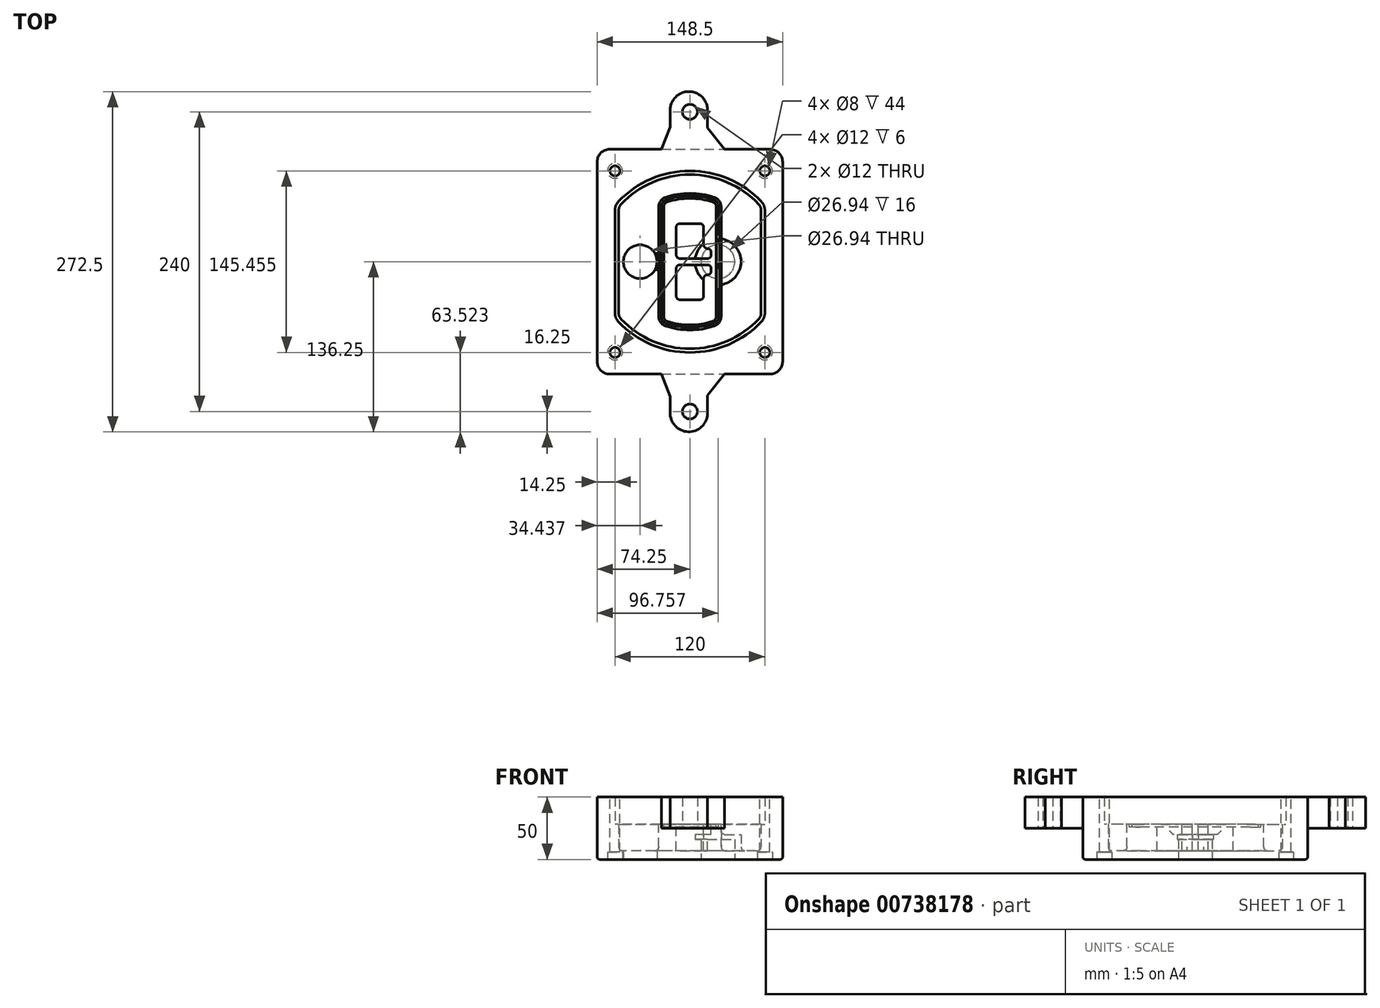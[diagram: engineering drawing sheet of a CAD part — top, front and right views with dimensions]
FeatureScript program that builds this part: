
annotation { "Feature Type Name" : "Feature", "Feature Type Description" : "" }
export const myFeature = defineFeature(function(context is Context, id is Id, definition is map)
    precondition{}
    {
        {
            var Q0;
            Q0=qCreatedBy(makeId("Top.planeOp"),FACE);
            var sketch = newSketch(context, id + "F0", { "sketchPlane" : qUnion([Q0])});
            skPoint(sketch, "E0.rect.middle", {"position": v(0, 0) * mm});
            skLineSegment(sketch, "E1.bottom", {"start": v(-64.25, -90) * mm, "end": v(64.25, -90) * mm});
            skLineSegment(sketch, "E1.top", {"start": v(-64.25, 90) * mm, "end": v(64.25, 90) * mm});
            skLineSegment(sketch, "E1.left", {"start": v(-74.25, -80) * mm, "end": v(-74.25, 80) * mm});
            skLineSegment(sketch, "E1.right", {"start": v(74.25, -80) * mm, "end": v(74.25, 80) * mm});
            skLineSegment(sketch, "E2", {"start": v(-74.25, 90) * mm, "end": v(74.25, -90) * mm, "construction": true});
            skLineSegment(sketch, "E3", {"start": v(74.25, 90) * mm, "end": v(-74.25, -90) * mm, "construction": true});
            skCircle(sketch, "E4", {"center": v(-60, 72.73) * mm, "radius": 4 * mm});
            skCircle(sketch, "E5", {"center": v(60, 72.73) * mm, "radius": 4 * mm});
            skCircle(sketch, "E6", {"center": v(60, -72.73) * mm, "radius": 4 * mm});
            skCircle(sketch, "E7", {"center": v(-60, -72.73) * mm, "radius": 4 * mm});
            skLineSegment(sketch, "E8", {"start": v(-60, 72.73) * mm, "end": v(60, 72.73) * mm, "construction": true});
            skLineSegment(sketch, "E9", {"start": v(60, 72.73) * mm, "end": v(60, -72.73) * mm, "construction": true});
            skLineSegment(sketch, "E10", {"start": v(60, -72.73) * mm, "end": v(-60, -72.73) * mm, "construction": true});
            skLineSegment(sketch, "E11", {"start": v(-60, -72.73) * mm, "end": v(-60, 72.73) * mm, "construction": true});
            skLineSegment(sketch, "E12", {"start": v(-60, 41.18) * mm, "end": v(-60, -41.18) * mm});
            skLineSegment(sketch, "E13", {"start": v(60, 41.18) * mm, "end": v(60, -41.18) * mm});
            skArc(sketch, "E14", {"start": v(57.27, 48.05) * mm, "mid": v(0, 72.73) * mm, "end": v(-57.27, 48.05) * mm});
            skArc(sketch, "E15", {"start": v(-57.27, -48.05) * mm, "mid": v(0, -72.73) * mm, "end": v(57.27, -48.05) * mm});
            skLineSegment(sketch, "E16", {"start": v(-60, 0) * mm, "end": v(60, 0) * mm, "construction": true});
            skPoint(sketch, "E17.visualSharp", {"position": v(-60, -45) * mm});
            skArc(sketch, "E17.filletArc", {"start": v(-60, -41.18) * mm, "mid": v(-59.3, -44.87) * mm, "end": v(-57.27, -48.05) * mm});
            skPoint(sketch, "E18.visualSharp", {"position": v(-60, 45) * mm});
            skArc(sketch, "E18.filletArc", {"start": v(-57.27, 48.05) * mm, "mid": v(-59.3, 44.87) * mm, "end": v(-60, 41.18) * mm});
            skPoint(sketch, "E19.visualSharp", {"position": v(60, 45) * mm});
            skArc(sketch, "E19.filletArc", {"start": v(60, 41.18) * mm, "mid": v(59.3, 44.87) * mm, "end": v(57.27, 48.05) * mm});
            skPoint(sketch, "E20.visualSharp", {"position": v(60, -45) * mm});
            skArc(sketch, "E20.filletArc", {"start": v(57.27, -48.05) * mm, "mid": v(59.3, -44.87) * mm, "end": v(60, -41.18) * mm});
            skPoint(sketch, "E21.visualSharp", {"position": v(-74.25, 90) * mm});
            skArc(sketch, "E21.filletArc", {"start": v(-64.25, 90) * mm, "mid": v(-71.32, 87.07) * mm, "end": v(-74.25, 80) * mm});
            skPoint(sketch, "E22.visualSharp", {"position": v(74.25, 90) * mm});
            skArc(sketch, "E22.filletArc", {"start": v(74.25, 80) * mm, "mid": v(71.32, 87.07) * mm, "end": v(64.25, 90) * mm});
            skPoint(sketch, "E23.visualSharp", {"position": v(74.25, -90) * mm});
            skArc(sketch, "E23.filletArc", {"start": v(64.25, -90) * mm, "mid": v(71.32, -87.07) * mm, "end": v(74.25, -80) * mm});
            skPoint(sketch, "E24.visualSharp", {"position": v(-74.25, -90) * mm});
            skArc(sketch, "E24.filletArc", {"start": v(-74.25, -80) * mm, "mid": v(-71.32, -87.07) * mm, "end": v(-64.25, -90) * mm});
            skArc(sketch, "E25.0", {"start": v(57, 41.18) * mm, "mid": v(56.5, 43.76) * mm, "end": v(55.09, 45.99) * mm});
            skLineSegment(sketch, "E25.1", {"start": v(57, 41.18) * mm, "end": v(57, -41.18) * mm});
            skArc(sketch, "E25.2", {"start": v(55.09, -45.99) * mm, "mid": v(56.5, -43.76) * mm, "end": v(57, -41.18) * mm});
            skArc(sketch, "E25.3", {"start": v(-55.09, -45.99) * mm, "mid": v(0, -69.73) * mm, "end": v(55.09, -45.99) * mm});
            skArc(sketch, "E25.4", {"start": v(-57, -41.18) * mm, "mid": v(-56.5, -43.76) * mm, "end": v(-55.09, -45.99) * mm});
            skArc(sketch, "E25.5", {"start": v(55.09, 45.99) * mm, "mid": v(0, 69.73) * mm, "end": v(-55.09, 45.99) * mm});
            skLineSegment(sketch, "E25.6", {"start": v(-57, 41.18) * mm, "end": v(-57, -41.18) * mm});
            skArc(sketch, "E25.7", {"start": v(-55.09, 45.99) * mm, "mid": v(-56.5, 43.76) * mm, "end": v(-57, 41.18) * mm});
            skArc(sketch, "E26.0", {"start": v(-60.18, 50.8) * mm, "mid": v(-63, 46.35) * mm, "end": v(-64, 41.18) * mm});
            skArc(sketch, "E26.1", {"start": v(60.18, 50.8) * mm, "mid": v(0, 76.73) * mm, "end": v(-60.18, 50.8) * mm});
            skArc(sketch, "E26.2", {"start": v(64, 41.18) * mm, "mid": v(63, 46.35) * mm, "end": v(60.18, 50.8) * mm});
            skLineSegment(sketch, "E26.3", {"start": v(64, 41.18) * mm, "end": v(64, -41.18) * mm});
            skArc(sketch, "E26.4", {"start": v(60.18, -50.8) * mm, "mid": v(63, -46.35) * mm, "end": v(64, -41.18) * mm});
            skLineSegment(sketch, "E26.5", {"start": v(-64, 41.18) * mm, "end": v(-64, -41.18) * mm});
            skArc(sketch, "E26.6", {"start": v(-60.18, -50.8) * mm, "mid": v(0, -76.73) * mm, "end": v(60.18, -50.8) * mm});
            skArc(sketch, "E26.7", {"start": v(-64, -41.18) * mm, "mid": v(-63, -46.35) * mm, "end": v(-60.18, -50.8) * mm});
            skSolve(sketch);
        }
        {
            var Q0;
            Q0=makeQuery(id+"F0.imprint","IMPRINT",FACE,{"disambiguationData":[TD([[makeQuery(id+"F0.imprint","IMPRINT",EDGE,{"derivedFrom":sQuery(id+"F0.wireOp",EDGE,"E1.bottom")}),1.0]])]});
            var Q1;
            Q1=makeQuery(id+"F0.imprint","IMPRINT",FACE,{"disambiguationData":[TD([[makeQuery(id+"F0.imprint","IMPRINT",EDGE,{"derivedFrom":sQuery(id+"F0.wireOp",EDGE,"E12")}),1.0]])]});
            var Q2;
            Q2=makeQuery(id+"F0.imprint","IMPRINT",FACE,{"disambiguationData":[TD([[makeQuery(id+"F0.imprint","IMPRINT",EDGE,{"derivedFrom":sQuery(id+"F0.wireOp",EDGE,"E25.0")}),1.0]])]});
            var Q3;
            Q3=makeQuery(id+"F0.imprint","IMPRINT",FACE,{"disambiguationData":[TD([[makeQuery(id+"F0.imprint","IMPRINT",EDGE,{"derivedFrom":sQuery(id+"F0.wireOp",EDGE,"E12")}),-1.0]])]});
            extrude(context, id + "F1", {"entities" : qUnion([Q0, Q1, Q2, Q3]), "oppositeDirection" : true, "depth" : 25 * mm});
        }
        {
            var Q0;
            Q0=makeQuery(id+"F0.imprint","IMPRINT",FACE,{"disambiguationData":[TD([[makeQuery(id+"F0.imprint","IMPRINT",EDGE,{"derivedFrom":sQuery(id+"F0.wireOp",EDGE,"E12")}),1.0]])]});
            extrude(context, id + "F2", {"entities" : qUnion([Q0]), "operationType" : NewBodyOperationType.ADD, "depth" : 3 * mm});
        }
        {
            var Q0;
            Q0=makeQuery(id+"F0.imprint","IMPRINT",FACE,{"disambiguationData":[TD([[makeQuery(id+"F0.imprint","IMPRINT",EDGE,{"derivedFrom":sQuery(id+"F0.wireOp",EDGE,"E25.0")}),1.0]])]});
            extrude(context, id + "F3", {"entities" : qUnion([Q0]), "operationType" : NewBodyOperationType.REMOVE, "oppositeDirection" : true, "depth" : 18 * mm});
        }
        {
            var Q0;
            Q0=makeQuery(id+"F2.opExtrude","CAP_FACE",FACE,{"disambiguationData":[OSD([sQuery(id+"F0.wireOp",EDGE,"E12"),sQuery(id+"F0.wireOp",EDGE,"E13"),sQuery(id+"F0.wireOp",EDGE,"E14"),sQuery(id+"F0.wireOp",EDGE,"E15"),sQuery(id+"F0.wireOp",EDGE,"E17.filletArc"),sQuery(id+"F0.wireOp",EDGE,"E18.filletArc"),sQuery(id+"F0.wireOp",EDGE,"E19.filletArc"),sQuery(id+"F0.wireOp",EDGE,"E20.filletArc"),sQuery(id+"F0.wireOp",EDGE,"E25.0"),sQuery(id+"F0.wireOp",EDGE,"E25.1"),sQuery(id+"F0.wireOp",EDGE,"E25.2"),sQuery(id+"F0.wireOp",EDGE,"E25.3"),sQuery(id+"F0.wireOp",EDGE,"E25.4"),sQuery(id+"F0.wireOp",EDGE,"E25.5"),sQuery(id+"F0.wireOp",EDGE,"E25.6"),sQuery(id+"F0.wireOp",EDGE,"E25.7")])],"isStart":false});
            var sketch = newSketch(context, id + "F4", { "sketchPlane" : qUnion([Q0])});
            skArc(sketch, "E27.0", {"start": v(-19.58, -51.49) * mm, "mid": v(0, -54.73) * mm, "end": v(19.58, -51.49) * mm});
            skArc(sketch, "E28.0", {"start": v(19.58, 51.49) * mm, "mid": v(0, 54.73) * mm, "end": v(-19.58, 51.49) * mm});
            skLineSegment(sketch, "E29", {"start": v(-25, 43.91) * mm, "end": v(-25, -43.91) * mm});
            skLineSegment(sketch, "E30", {"start": v(25, 43.91) * mm, "end": v(25, -43.91) * mm});
            skLineSegment(sketch, "E31", {"start": v(-25, 49.35) * mm, "end": v(25, 49.35) * mm, "construction": true});
            skLineSegment(sketch, "E32", {"start": v(-25, -49.35) * mm, "end": v(25, -49.35) * mm, "construction": true});
            skPoint(sketch, "E33.visualSharp", {"position": v(-25, 49.35) * mm});
            skArc(sketch, "E33.filletArc", {"start": v(-19.58, 51.49) * mm, "mid": v(-23.5, 48.57) * mm, "end": v(-25, 43.91) * mm});
            skPoint(sketch, "E34.visualSharp", {"position": v(25, 49.35) * mm});
            skArc(sketch, "E34.filletArc", {"start": v(25, 43.91) * mm, "mid": v(23.5, 48.57) * mm, "end": v(19.58, 51.49) * mm});
            skPoint(sketch, "E35.visualSharp", {"position": v(25, -49.35) * mm});
            skArc(sketch, "E35.filletArc", {"start": v(19.58, -51.49) * mm, "mid": v(23.5, -48.57) * mm, "end": v(25, -43.91) * mm});
            skPoint(sketch, "E36.visualSharp", {"position": v(-25, -49.35) * mm});
            skArc(sketch, "E36.filletArc", {"start": v(-25, -43.91) * mm, "mid": v(-23.5, -48.57) * mm, "end": v(-19.58, -51.49) * mm});
            skArc(sketch, "E37.0", {"start": v(55.09, 45.99) * mm, "mid": v(0, 69.73) * mm, "end": v(-55.09, 45.99) * mm});
            skArc(sketch, "E37.1", {"start": v(-55.09, 45.99) * mm, "mid": v(-56.5, 43.76) * mm, "end": v(-57, 41.18) * mm});
            skLineSegment(sketch, "E37.2", {"start": v(-57, 41.18) * mm, "end": v(-57, -41.18) * mm});
            skArc(sketch, "E37.3", {"start": v(-57, -41.18) * mm, "mid": v(-56.5, -43.76) * mm, "end": v(-55.09, -45.99) * mm});
            skArc(sketch, "E37.4", {"start": v(-55.09, -45.99) * mm, "mid": v(0, -69.73) * mm, "end": v(55.09, -45.99) * mm});
            skArc(sketch, "E37.5", {"start": v(55.09, -45.99) * mm, "mid": v(56.5, -43.76) * mm, "end": v(57, -41.18) * mm});
            skLineSegment(sketch, "E37.6", {"start": v(57, 41.18) * mm, "end": v(57, -41.18) * mm});
            skArc(sketch, "E37.7", {"start": v(57, 41.18) * mm, "mid": v(56.5, 43.76) * mm, "end": v(55.09, 45.99) * mm});
            skLineSegment(sketch, "E38.0", {"start": v(23, 43.91) * mm, "end": v(23, -43.91) * mm});
            skArc(sketch, "E38.1", {"start": v(18.93, -49.6) * mm, "mid": v(21.88, -47.4) * mm, "end": v(23, -43.91) * mm});
            skArc(sketch, "E38.2", {"start": v(-18.93, -49.6) * mm, "mid": v(0, -52.73) * mm, "end": v(18.93, -49.6) * mm});
            skArc(sketch, "E38.3", {"start": v(-23, -43.91) * mm, "mid": v(-21.88, -47.4) * mm, "end": v(-18.93, -49.6) * mm});
            skLineSegment(sketch, "E38.4", {"start": v(-23, 43.91) * mm, "end": v(-23, -43.91) * mm});
            skArc(sketch, "E38.5", {"start": v(23, 43.91) * mm, "mid": v(21.88, 47.4) * mm, "end": v(18.93, 49.6) * mm});
            skArc(sketch, "E38.6", {"start": v(-18.93, 49.6) * mm, "mid": v(-21.88, 47.4) * mm, "end": v(-23, 43.91) * mm});
            skArc(sketch, "E38.7", {"start": v(18.93, 49.6) * mm, "mid": v(0, 52.73) * mm, "end": v(-18.93, 49.6) * mm});
            skArc(sketch, "E39.0", {"start": v(21, 43.91) * mm, "mid": v(20.25, 46.24) * mm, "end": v(18.29, 47.7) * mm});
            skLineSegment(sketch, "E39.1", {"start": v(21, 43.91) * mm, "end": v(21, -43.91) * mm});
            skArc(sketch, "E39.2", {"start": v(18.29, -47.7) * mm, "mid": v(20.25, -46.24) * mm, "end": v(21, -43.91) * mm});
            skArc(sketch, "E39.3", {"start": v(-18.29, -47.7) * mm, "mid": v(0, -50.73) * mm, "end": v(18.29, -47.7) * mm});
            skArc(sketch, "E39.4", {"start": v(-21, -43.91) * mm, "mid": v(-20.25, -46.24) * mm, "end": v(-18.29, -47.7) * mm});
            skArc(sketch, "E39.5", {"start": v(18.29, 47.7) * mm, "mid": v(0, 50.73) * mm, "end": v(-18.29, 47.7) * mm});
            skLineSegment(sketch, "E39.6", {"start": v(-21, 43.91) * mm, "end": v(-21, -43.91) * mm});
            skArc(sketch, "E39.7", {"start": v(-18.29, 47.7) * mm, "mid": v(-20.25, 46.24) * mm, "end": v(-21, 43.91) * mm});
            skLineSegment(sketch, "E40", {"start": v(-25, 0) * mm, "end": v(25, 0) * mm, "construction": true});
            skLineSegment(sketch, "E41", {"start": v(-11, 5.5) * mm, "end": v(-11, 27.5) * mm});
            skLineSegment(sketch, "E42", {"start": v(-8, 30.5) * mm, "end": v(8, 30.5) * mm});
            skLineSegment(sketch, "E43", {"start": v(11, 27.5) * mm, "end": v(11, 13.5) * mm});
            skLineSegment(sketch, "E44", {"start": v(14, 10.5) * mm, "end": v(14, 10.5) * mm});
            skLineSegment(sketch, "E45", {"start": v(17, 7.5) * mm, "end": v(17, 5.5) * mm});
            skLineSegment(sketch, "E46", {"start": v(14, 2.5) * mm, "end": v(-8, 2.5) * mm});
            skPoint(sketch, "E47.visualSharp", {"position": v(-11, 30.5) * mm});
            skArc(sketch, "E47.filletArc", {"start": v(-8, 30.5) * mm, "mid": v(-10.12, 29.62) * mm, "end": v(-11, 27.5) * mm});
            skPoint(sketch, "E48.visualSharp", {"position": v(11, 30.5) * mm});
            skArc(sketch, "E48.filletArc", {"start": v(11, 27.5) * mm, "mid": v(10.12, 29.62) * mm, "end": v(8, 30.5) * mm});
            skPoint(sketch, "E49.visualSharp", {"position": v(11, 10.5) * mm});
            skArc(sketch, "E49.filletArc", {"start": v(11, 13.5) * mm, "mid": v(11.88, 11.38) * mm, "end": v(14, 10.5) * mm});
            skPoint(sketch, "E50.visualSharp", {"position": v(17, 10.5) * mm});
            skArc(sketch, "E50.filletArc", {"start": v(17, 7.5) * mm, "mid": v(16.12, 9.62) * mm, "end": v(14, 10.5) * mm});
            skPoint(sketch, "E51.visualSharp", {"position": v(17, 2.5) * mm});
            skArc(sketch, "E51.filletArc", {"start": v(14, 2.5) * mm, "mid": v(16.12, 3.38) * mm, "end": v(17, 5.5) * mm});
            skPoint(sketch, "E52.visualSharp", {"position": v(-11, 2.5) * mm});
            skArc(sketch, "E52.filletArc", {"start": v(-11, 5.5) * mm, "mid": v(-10.12, 3.38) * mm, "end": v(-8, 2.5) * mm});
            skLineSegment(sketch, "E53.0.MirrorCS", {"start": v(14, -2.5) * mm, "end": v(-8, -2.5) * mm});
            skArc(sketch, "E54.0.MirrorCS", {"start": v(-11, -5.5) * mm, "mid": v(-10.12, -3.38) * mm, "end": v(-8, -2.5) * mm});
            skLineSegment(sketch, "E55.0.MirrorCS", {"start": v(-11, -5.5) * mm, "end": v(-11, -27.5) * mm});
            skArc(sketch, "E56.0.MirrorCS", {"start": v(-8, -30.5) * mm, "mid": v(-10.12, -29.62) * mm, "end": v(-11, -27.5) * mm});
            skLineSegment(sketch, "E57.0.MirrorCS", {"start": v(-8, -30.5) * mm, "end": v(8, -30.5) * mm});
            skArc(sketch, "E58.0.MirrorCS", {"start": v(11, -27.5) * mm, "mid": v(10.12, -29.62) * mm, "end": v(8, -30.5) * mm});
            skLineSegment(sketch, "E59.0.MirrorCS", {"start": v(11, -27.5) * mm, "end": v(11, -13.5) * mm});
            skArc(sketch, "E60.0.MirrorCS", {"start": v(11, -13.5) * mm, "mid": v(11.88, -11.38) * mm, "end": v(14, -10.5) * mm});
            skArc(sketch, "E61.0.MirrorCS", {"start": v(17, -7.5) * mm, "mid": v(16.12, -9.62) * mm, "end": v(14, -10.5) * mm});
            skLineSegment(sketch, "E62.0.MirrorCS", {"start": v(17, -7.5) * mm, "end": v(17, -5.5) * mm});
            skArc(sketch, "E63.0.MirrorCS", {"start": v(14, -2.5) * mm, "mid": v(16.12, -3.38) * mm, "end": v(17, -5.5) * mm});
            skSolve(sketch);
        }
        {
            var Q0;
            Q0=makeQuery(id+"F4.imprint","IMPRINT",FACE,{"disambiguationData":[TD([[makeQuery(id+"F4.imprint","IMPRINT",EDGE,{"derivedFrom":sQuery(id+"F4.wireOp",EDGE,"E27.0")}),1.0]])]});
            var Q1;
            Q1=makeQuery(id+"F4.imprint","IMPRINT",FACE,{"disambiguationData":[TD([[makeQuery(id+"F4.imprint","IMPRINT",EDGE,{"derivedFrom":sQuery(id+"F4.wireOp",EDGE,"E38.0")}),-1.0]])]});
            var Q2;
            Q2=makeQuery(id+"F4.imprint","IMPRINT",FACE,{"disambiguationData":[TD([[makeQuery(id+"F4.imprint","IMPRINT",EDGE,{"derivedFrom":sQuery(id+"F4.wireOp",EDGE,"E39.0")}),1.0]])]});
            extrude(context, id + "F5", {"entities" : qUnion([Q0, Q1, Q2]), "operationType" : NewBodyOperationType.ADD, "endBound" : BoundingType.UP_TO_NEXT, "oppositeDirection" : true, "depth" : 25 * mm});
        }
        {
            var Q0;
            Q0=makeQuery(id+"F4.imprint","IMPRINT",FACE,{"disambiguationData":[TD([[makeQuery(id+"F4.imprint","IMPRINT",EDGE,{"derivedFrom":sQuery(id+"F4.wireOp",EDGE,"E38.0")}),-1.0]])]});
            extrude(context, id + "F6", {"entities" : qUnion([Q0]), "operationType" : NewBodyOperationType.REMOVE, "oppositeDirection" : true, "depth" : 2 * mm});
        }
        {
            var Q0;
            Q0=makeQuery(id+"F1.opExtrude","CAP_FACE",FACE,{"disambiguationData":[OSD([sQuery(id+"F0.wireOp",EDGE,"E1.bottom"),sQuery(id+"F0.wireOp",EDGE,"E1.top"),sQuery(id+"F0.wireOp",EDGE,"E1.left"),sQuery(id+"F0.wireOp",EDGE,"E1.right"),sQuery(id+"F0.wireOp",EDGE,"E4"),sQuery(id+"F0.wireOp",EDGE,"E5"),sQuery(id+"F0.wireOp",EDGE,"E6"),sQuery(id+"F0.wireOp",EDGE,"E7"),sQuery(id+"F0.wireOp",EDGE,"E21.filletArc"),sQuery(id+"F0.wireOp",EDGE,"E22.filletArc"),sQuery(id+"F0.wireOp",EDGE,"E23.filletArc"),sQuery(id+"F0.wireOp",EDGE,"E24.filletArc")])],"isStart":false});
            var sketch = newSketch(context, id + "F7", { "sketchPlane" : qUnion([Q0])});
            skCircle(sketch, "E64", {"center": v(22.5, 0) * mm, "radius": 13.47 * mm});
            skCircle(sketch, "E65", {"center": v(-39.81, 0) * mm, "radius": 13.47 * mm});
            skLineSegment(sketch, "E66", {"start": v(74.25, 0) * mm, "end": v(-74.25, 0) * mm});
            skCircle(sketch, "E67", {"center": v(22.5, 0) * mm, "radius": 18.47 * mm});
            skCircle(sketch, "E68", {"center": v(60, -72.73) * mm, "radius": 6 * mm});
            skCircle(sketch, "E69", {"center": v(-60, -72.73) * mm, "radius": 6 * mm});
            skCircle(sketch, "E70", {"center": v(-60, 72.73) * mm, "radius": 6 * mm});
            skCircle(sketch, "E71", {"center": v(60, 72.73) * mm, "radius": 6 * mm});
            skSolve(sketch);
        }
        {
            var Q0;
            {var subQ1=sQuery(id+"F7.wireOp",EDGE,"E66");var subQ4=sQuery(id+"F7.wireOp",EDGE,"E64");var subQ6=makeQuery(id+"F7.imprint","INTERSECT",VERTEX,{"disambiguationData":[OD(0.0)],"derivedFrom":[subQ4,subQ1]});Q0=makeQuery(id+"F7.imprint","IMPRINT",FACE,{"disambiguationData":[TD([[makeQuery(id+"F7.imprint","IMPRINT",EDGE,{"disambiguationData":[TD([[subQ6,-1.0]])],"derivedFrom":subQ4}),-1.0]])]});}
            var Q1;
            {var subQ0=sQuery(id+"F7.wireOp",EDGE,"E66");var subQ1=sQuery(id+"F7.wireOp",EDGE,"E64");var subQ3=makeQuery(id+"F7.imprint","INTERSECT",VERTEX,{"disambiguationData":[OD(0.0)],"derivedFrom":[subQ1,subQ0]});Q1=makeQuery(id+"F7.imprint","IMPRINT",FACE,{"disambiguationData":[TD([[makeQuery(id+"F7.imprint","IMPRINT",EDGE,{"disambiguationData":[TD([[subQ3,-1.0]])],"derivedFrom":subQ1}),1.0]])]});}
            var Q2;
            {var subQ0=sQuery(id+"F7.wireOp",EDGE,"E66");var subQ1=sQuery(id+"F7.wireOp",EDGE,"E64");var subQ3=makeQuery(id+"F7.imprint","INTERSECT",VERTEX,{"disambiguationData":[OD(0.0)],"derivedFrom":[subQ1,subQ0]});Q2=makeQuery(id+"F7.imprint","IMPRINT",FACE,{"disambiguationData":[TD([[makeQuery(id+"F7.imprint","IMPRINT",EDGE,{"disambiguationData":[TD([[subQ3,1.0]])],"derivedFrom":subQ1}),1.0]])]});}
            var Q3;
            {var subQ1=sQuery(id+"F7.wireOp",EDGE,"E66");var subQ4=sQuery(id+"F7.wireOp",EDGE,"E64");var subQ6=makeQuery(id+"F7.imprint","INTERSECT",VERTEX,{"disambiguationData":[OD(0.0)],"derivedFrom":[subQ4,subQ1]});Q3=makeQuery(id+"F7.imprint","IMPRINT",FACE,{"disambiguationData":[TD([[makeQuery(id+"F7.imprint","IMPRINT",EDGE,{"disambiguationData":[TD([[subQ6,1.0]])],"derivedFrom":subQ4}),-1.0]])]});}
            extrude(context, id + "F8", {"entities" : qUnion([Q0, Q1, Q2, Q3]), "operationType" : NewBodyOperationType.ADD, "oppositeDirection" : true, "depth" : 20 * mm});
        }
        {
            var Q0;
            {var subQ0=sQuery(id+"F7.wireOp",EDGE,"E66");var subQ1=sQuery(id+"F7.wireOp",EDGE,"E64");var subQ3=makeQuery(id+"F7.imprint","INTERSECT",VERTEX,{"disambiguationData":[OD(0.0)],"derivedFrom":[subQ1,subQ0]});Q0=makeQuery(id+"F7.imprint","IMPRINT",FACE,{"disambiguationData":[TD([[makeQuery(id+"F7.imprint","IMPRINT",EDGE,{"disambiguationData":[TD([[subQ3,-1.0]])],"derivedFrom":subQ1}),1.0]])]});}
            var Q1;
            {var subQ0=sQuery(id+"F7.wireOp",EDGE,"E66");var subQ1=sQuery(id+"F7.wireOp",EDGE,"E64");var subQ3=makeQuery(id+"F7.imprint","INTERSECT",VERTEX,{"disambiguationData":[OD(0.0)],"derivedFrom":[subQ1,subQ0]});Q1=makeQuery(id+"F7.imprint","IMPRINT",FACE,{"disambiguationData":[TD([[makeQuery(id+"F7.imprint","IMPRINT",EDGE,{"disambiguationData":[TD([[subQ3,1.0]])],"derivedFrom":subQ1}),1.0]])]});}
            extrude(context, id + "F9", {"entities" : qUnion([Q0, Q1]), "operationType" : NewBodyOperationType.REMOVE, "oppositeDirection" : true, "depth" : 16 * mm});
        }
        {
            var Q0;
            {var subQ0=sQuery(id+"F7.wireOp",EDGE,"E66");var subQ1=sQuery(id+"F7.wireOp",EDGE,"E65");var subQ3=makeQuery(id+"F7.imprint","INTERSECT",VERTEX,{"disambiguationData":[OD(0.0)],"derivedFrom":[subQ1,subQ0]});Q0=makeQuery(id+"F7.imprint","IMPRINT",FACE,{"disambiguationData":[TD([[makeQuery(id+"F7.imprint","IMPRINT",EDGE,{"disambiguationData":[TD([[subQ3,-1.0]])],"derivedFrom":subQ1}),1.0]])]});}
            var Q1;
            {var subQ0=sQuery(id+"F7.wireOp",EDGE,"E66");var subQ1=sQuery(id+"F7.wireOp",EDGE,"E65");var subQ3=makeQuery(id+"F7.imprint","INTERSECT",VERTEX,{"disambiguationData":[OD(0.0)],"derivedFrom":[subQ1,subQ0]});Q1=makeQuery(id+"F7.imprint","IMPRINT",FACE,{"disambiguationData":[TD([[makeQuery(id+"F7.imprint","IMPRINT",EDGE,{"disambiguationData":[TD([[subQ3,1.0]])],"derivedFrom":subQ1}),1.0]])]});}
            extrude(context, id + "F10", {"entities" : qUnion([Q0, Q1]), "operationType" : NewBodyOperationType.REMOVE, "oppositeDirection" : true, "depth" : 25 * mm});
        }
        {
            var Q0;
            Q0=makeQuery(id+"F7.imprint","IMPRINT",FACE,{"disambiguationData":[TD([[makeQuery(id+"F7.imprint","IMPRINT",EDGE,{"derivedFrom":sQuery(id+"F7.wireOp",EDGE,"E68")}),1.0]])]});
            var Q1;
            Q1=makeQuery(id+"F7.imprint","IMPRINT",FACE,{"disambiguationData":[TD([[makeQuery(id+"F7.imprint","IMPRINT",EDGE,{"derivedFrom":makeQuery(id+"F1.opExtrude","CAP_EDGE",EDGE,{"disambiguationData":[OSD([sQuery(id+"F0.wireOp",EDGE,"E5")])],"isStart":false})}),-1.0]])]});
            var Q2;
            Q2=makeQuery(id+"F7.imprint","IMPRINT",FACE,{"disambiguationData":[TD([[makeQuery(id+"F7.imprint","IMPRINT",EDGE,{"derivedFrom":sQuery(id+"F7.wireOp",EDGE,"E69")}),1.0]])]});
            var Q3;
            Q3=makeQuery(id+"F7.imprint","IMPRINT",FACE,{"disambiguationData":[TD([[makeQuery(id+"F7.imprint","IMPRINT",EDGE,{"derivedFrom":makeQuery(id+"F1.opExtrude","CAP_EDGE",EDGE,{"disambiguationData":[OSD([sQuery(id+"F0.wireOp",EDGE,"E4")])],"isStart":false})}),-1.0]])]});
            var Q4;
            Q4=makeQuery(id+"F7.imprint","IMPRINT",FACE,{"disambiguationData":[TD([[makeQuery(id+"F7.imprint","IMPRINT",EDGE,{"derivedFrom":sQuery(id+"F7.wireOp",EDGE,"E70")}),1.0]])]});
            var Q5;
            Q5=makeQuery(id+"F7.imprint","IMPRINT",FACE,{"disambiguationData":[TD([[makeQuery(id+"F7.imprint","IMPRINT",EDGE,{"derivedFrom":makeQuery(id+"F1.opExtrude","CAP_EDGE",EDGE,{"disambiguationData":[OSD([sQuery(id+"F0.wireOp",EDGE,"E7")])],"isStart":false})}),-1.0]])]});
            var Q6;
            Q6=makeQuery(id+"F7.imprint","IMPRINT",FACE,{"disambiguationData":[TD([[makeQuery(id+"F7.imprint","IMPRINT",EDGE,{"derivedFrom":sQuery(id+"F7.wireOp",EDGE,"E71")}),1.0]])]});
            var Q7;
            Q7=makeQuery(id+"F7.imprint","IMPRINT",FACE,{"disambiguationData":[TD([[makeQuery(id+"F7.imprint","IMPRINT",EDGE,{"derivedFrom":makeQuery(id+"F1.opExtrude","CAP_EDGE",EDGE,{"disambiguationData":[OSD([sQuery(id+"F0.wireOp",EDGE,"E6")])],"isStart":false})}),-1.0]])]});
            extrude(context, id + "F11", {"entities" : qUnion([Q0, Q1, Q2, Q3, Q4, Q5, Q6, Q7]), "operationType" : NewBodyOperationType.REMOVE, "oppositeDirection" : true, "depth" : 6 * mm});
        }
        {
            var Q0;
            Q0=makeQuery(id+"F9.boolean.opBoolean","COPY",FACE,{"derivedFrom":makeQuery(id+"F9.opExtrude","CAP_FACE",FACE,{"disambiguationData":[OSD([sQuery(id+"F7.wireOp",EDGE,"E64")])],"isStart":false})});
            var sketch = newSketch(context, id + "F12", { "sketchPlane" : qUnion([Q0])});
            skArc(sketch, "E72.0", {"start": v(11, 14.45) * mm, "mid": v(6.45, 9.13) * mm, "end": v(4.2, 2.5) * mm});
            skArc(sketch, "E72.1", {"start": v(4.2, -2.5) * mm, "mid": v(6.45, -9.13) * mm, "end": v(11, -14.45) * mm});
            skLineSegment(sketch, "E73", {"start": v(4.2, -2.5) * mm, "end": v(14, -2.5) * mm});
            skLineSegment(sketch, "E74.0", {"start": v(14, 2.5) * mm, "end": v(4.2, 2.5) * mm});
            skArc(sketch, "E74.1", {"start": v(14, 2.5) * mm, "mid": v(16.12, 3.38) * mm, "end": v(17, 5.5) * mm});
            skLineSegment(sketch, "E74.2", {"start": v(17, 7.5) * mm, "end": v(17, 5.5) * mm});
            skArc(sketch, "E74.3", {"start": v(17, 7.5) * mm, "mid": v(16.12, 9.62) * mm, "end": v(14, 10.5) * mm});
            skArc(sketch, "E74.4", {"start": v(11, 13.5) * mm, "mid": v(11.88, 11.38) * mm, "end": v(14, 10.5) * mm});
            skLineSegment(sketch, "E74.5", {"start": v(11, 14.45) * mm, "end": v(11, 13.5) * mm});
            skLineSegment(sketch, "E74.7", {"start": v(14, -2.5) * mm, "end": v(4.2, -2.5) * mm});
            skArc(sketch, "E74.8", {"start": v(14, -2.5) * mm, "mid": v(16.12, -3.38) * mm, "end": v(17, -5.5) * mm});
            skLineSegment(sketch, "E74.9", {"start": v(17, -7.5) * mm, "end": v(17, -5.5) * mm});
            skArc(sketch, "E74.10", {"start": v(17, -7.5) * mm, "mid": v(16.12, -9.62) * mm, "end": v(14, -10.5) * mm});
            skArc(sketch, "E74.11", {"start": v(11, -13.5) * mm, "mid": v(11.88, -11.38) * mm, "end": v(14, -10.5) * mm});
            skLineSegment(sketch, "E74.12", {"start": v(11, -14.45) * mm, "end": v(11, -13.5) * mm});
            skPoint(sketch, "E75.orphan", {"position": v(11, -27.5) * mm});
            skPoint(sketch, "E76.orphan", {"position": v(-8, -2.5) * mm});
            skPoint(sketch, "E77.orphan", {"position": v(-8, 2.5) * mm});
            skPoint(sketch, "E78.orphan", {"position": v(11, 27.5) * mm});
            skSolve(sketch);
        }
        {
            var Q0;
            {var subQ7=sQuery(id+"F12.wireOp",EDGE,"E72.0");var subQ14=sQuery(id+"F12.wireOp",EDGE,"E72.1");var subQ16=sQuery(id+"F12.wireOp",EDGE,"E74.1");var subQ18=sQuery(id+"F12.wireOp",EDGE,"E74.8");Q0=qUnion([makeQuery(id+"F12.imprint","IMPRINT",FACE,{"disambiguationData":[TD([[makeQuery(id+"F12.imprint","IMPRINT",EDGE,{"derivedFrom":subQ7}),1.0]])]}),makeQuery(id+"F12.imprint","IMPRINT",FACE,{"disambiguationData":[TD([[makeQuery(id+"F12.imprint","IMPRINT",EDGE,{"derivedFrom":subQ14}),1.0]])]}),makeQuery(id+"F12.imprint","IMPRINT",FACE,{"disambiguationData":[TD([[makeQuery(id+"F12.imprint","IMPRINT",EDGE,{"derivedFrom":subQ16}),1.0]])]}),makeQuery(id+"F12.imprint","IMPRINT",FACE,{"disambiguationData":[TD([[makeQuery(id+"F12.imprint","IMPRINT",EDGE,{"derivedFrom":subQ18}),-1.0]])]})]);}
            var Q1;
            Q1=makeQuery(id+"F5.boolean.opBoolean","SPLIT",FACE,{"disambiguationData":[TD([makeQuery(id+"F5.opExtrude","SWEPT_FACE",FACE,{"disambiguationData":[OSD([sQuery(id+"F4.wireOp",EDGE,"E41")])]})])],"derivedFrom":makeQuery(id+"F3.boolean.opBoolean","COPY",FACE,{"derivedFrom":makeQuery(id+"F3.opExtrude","CAP_FACE",FACE,{"disambiguationData":[OSD([sQuery(id+"F0.wireOp",EDGE,"E25.0"),sQuery(id+"F0.wireOp",EDGE,"E25.1"),sQuery(id+"F0.wireOp",EDGE,"E25.2"),sQuery(id+"F0.wireOp",EDGE,"E25.3"),sQuery(id+"F0.wireOp",EDGE,"E25.4"),sQuery(id+"F0.wireOp",EDGE,"E25.5"),sQuery(id+"F0.wireOp",EDGE,"E25.6"),sQuery(id+"F0.wireOp",EDGE,"E25.7")])],"isStart":false})})});
            extrude(context, id + "F13", {"entities" : qUnion([Q0]), "operationType" : NewBodyOperationType.REMOVE, "endBound" : BoundingType.UP_TO_SURFACE, "endBoundEntityFace" : qUnion([Q1]), "depth" : 25 * mm});
        }
        {
            var Q0;
            Q0=makeQuery(id+"F3.boolean.opBoolean","COPY",EDGE,{"derivedFrom":makeQuery(id+"F3.opExtrude","CAP_EDGE",EDGE,{"disambiguationData":[OSD([sQuery(id+"F0.wireOp",EDGE,"E25.6")])],"isStart":false})});
            var Q1;
            Q1=makeQuery(id+"F8.boolean.opBoolean","INTERSECT",EDGE,{"derivedFrom":[makeQuery(id+"F5.opExtrude","SWEPT_FACE",FACE,{"disambiguationData":[OSD([sQuery(id+"F4.wireOp",EDGE,"E30")])]}),makeQuery(id+"F8.opExtrude","CAP_FACE",FACE,{"disambiguationData":[OSD([sQuery(id+"F7.wireOp",EDGE,"E67")])],"isStart":false})]});
            var Q2;
            Q2=makeQuery(id+"F8.boolean.opBoolean","INTERSECT",EDGE,{"disambiguationData":[OD(1.0)],"derivedFrom":[makeQuery(id+"F5.opExtrude","SWEPT_FACE",FACE,{"disambiguationData":[OSD([sQuery(id+"F4.wireOp",EDGE,"E30")])]}),makeQuery(id+"F8.opExtrude","SWEPT_FACE",FACE,{"disambiguationData":[OSD([sQuery(id+"F7.wireOp",EDGE,"E67")])]})]});
            var Q3;
            {var subQ0=sQuery(id+"F4.wireOp",EDGE,"E30");Q3=makeQuery(id+"F8.boolean.opBoolean","SPLIT",EDGE,{"disambiguationData":[TD([makeQuery(id+"F5.opExtrude","SWEPT_FACE",FACE,{"disambiguationData":[OSD([sQuery(id+"F4.wireOp",EDGE,"E35.filletArc")])]})])],"derivedFrom":makeQuery(id+"F5.opExtrude","CAP_EDGE",EDGE,{"disambiguationData":[OSD([subQ0])],"isStart":false})});}
            var Q4;
            {var subQ0=sQuery(id+"F0.wireOp",EDGE,"E25.7");var subQ1=sQuery(id+"F0.wireOp",EDGE,"E25.1");var subQ2=sQuery(id+"F0.wireOp",EDGE,"E25.6");var subQ3=sQuery(id+"F0.wireOp",EDGE,"E25.5");var subQ4=sQuery(id+"F0.wireOp",EDGE,"E25.4");var subQ5=sQuery(id+"F0.wireOp",EDGE,"E25.0");var subQ6=sQuery(id+"F0.wireOp",EDGE,"E25.2");var subQ7=sQuery(id+"F0.wireOp",EDGE,"E25.3");Q4=makeQuery(id+"F8.boolean.opBoolean","INTERSECT",EDGE,{"derivedFrom":[makeQuery(id+"F5.boolean.opBoolean","SPLIT",FACE,{"disambiguationData":[TD([makeQuery(id+"F2.opExtrude","SWEPT_FACE",FACE,{"disambiguationData":[OSD([subQ5])]})])],"derivedFrom":makeQuery(id+"F3.boolean.opBoolean","COPY",FACE,{"derivedFrom":makeQuery(id+"F3.opExtrude","CAP_FACE",FACE,{"disambiguationData":[OSD([subQ5,subQ1,subQ6,subQ7,subQ4,subQ3,subQ2,subQ0])],"isStart":false})})}),makeQuery(id+"F8.opExtrude","SWEPT_FACE",FACE,{"disambiguationData":[OSD([sQuery(id+"F7.wireOp",EDGE,"E67")])]})]});}
            var Q5;
            Q5=makeQuery(id+"F8.boolean.opBoolean","INTERSECT",EDGE,{"disambiguationData":[OD(0.0)],"derivedFrom":[makeQuery(id+"F5.opExtrude","SWEPT_FACE",FACE,{"disambiguationData":[OSD([sQuery(id+"F4.wireOp",EDGE,"E30")])]}),makeQuery(id+"F8.opExtrude","SWEPT_FACE",FACE,{"disambiguationData":[OSD([sQuery(id+"F7.wireOp",EDGE,"E67")])]})]});
            fillet(context, id + "F14", {"entities" : qUnion([Q0, Q1, Q2, Q3, Q4, Q5]), "radius" : 3 * mm, "tangentPropagation" : true, "allowEdgeOverflow" : false});
        }
        {
            var Q0;
            Q0=makeQuery(id+"F1.opExtrude","CAP_EDGE",EDGE,{"disambiguationData":[OSD([sQuery(id+"F0.wireOp",EDGE,"E1.bottom")])],"isStart":false});
            fillet(context, id + "F15", {"entities" : qUnion([Q0]), "radius" : 2 * mm, "tangentPropagation" : true, "allowEdgeOverflow" : false});
        }
        {
            var Q0;
            {var subQ0=sQuery(id+"F0.wireOp",EDGE,"E21.filletArc");var subQ1=sQuery(id+"F0.wireOp",EDGE,"E7");var subQ2=sQuery(id+"F0.wireOp",EDGE,"E6");var subQ3=sQuery(id+"F0.wireOp",EDGE,"E5");var subQ4=sQuery(id+"F0.wireOp",EDGE,"E4");var subQ5=sQuery(id+"F0.wireOp",EDGE,"E22.filletArc");var subQ6=sQuery(id+"F0.wireOp",EDGE,"E1.bottom");var subQ7=sQuery(id+"F0.wireOp",EDGE,"E1.right");var subQ8=sQuery(id+"F0.wireOp",EDGE,"E1.top");var subQ9=sQuery(id+"F0.wireOp",EDGE,"E1.left");var subQ10=sQuery(id+"F0.wireOp",EDGE,"E23.filletArc");var subQ11=sQuery(id+"F0.wireOp",EDGE,"E24.filletArc");Q0=makeQuery(id+"F2.boolean.opBoolean","SPLIT",FACE,{"disambiguationData":[TD([makeQuery(id+"F1.opExtrude","SWEPT_FACE",FACE,{"disambiguationData":[OSD([subQ6])]})])],"derivedFrom":makeQuery(id+"F1.opExtrude","CAP_FACE",FACE,{"disambiguationData":[OSD([subQ6,subQ8,subQ9,subQ7,subQ4,subQ3,subQ2,subQ1,subQ0,subQ5,subQ10,subQ11])],"isStart":true})});}
            var sketch = newSketch(context, id + "F16", { "sketchPlane" : qUnion([Q0])});
            skLineSegment(sketch, "E79", {"start": v(0, 90) * mm, "end": v(0, 120) * mm, "construction": true});
            skCircle(sketch, "E80", {"center": v(0, 120) * mm, "radius": 6 * mm});
            skLineSegment(sketch, "E81", {"start": v(-22.74, 90) * mm, "end": v(-15.8, 108) * mm});
            skLineSegment(sketch, "E82", {"start": v(27.8, 90) * mm, "end": v(14.13, 107.09) * mm});
            skLineSegment(sketch, "E83", {"start": v(14.13, 107.09) * mm, "end": v(14.13, 120.3) * mm});
            skLineSegment(sketch, "E84", {"start": v(-15.8, 108) * mm, "end": v(-15.8, 122.2) * mm});
            skArc(sketch, "E85", {"start": v(14.13, 120.3) * mm, "mid": v(0.12, 136.22) * mm, "end": v(-15.8, 122.2) * mm});
            skLineSegment(sketch, "E86", {"start": v(-74.25, 0) * mm, "end": v(74.25, 0) * mm});
            skLineSegment(sketch, "E87.MirrorCS", {"start": v(-22.74, -90) * mm, "end": v(-15.8, -108) * mm});
            skLineSegment(sketch, "E88.MirrorCS", {"start": v(0, -90) * mm, "end": v(0, -120) * mm, "construction": true});
            skLineSegment(sketch, "E89.MirrorCS", {"start": v(27.8, -90) * mm, "end": v(14.13, -107.09) * mm});
            skLineSegment(sketch, "E90.MirrorCS", {"start": v(14.13, -107.09) * mm, "end": v(14.13, -120.3) * mm});
            skLineSegment(sketch, "E91.MirrorCS", {"start": v(-15.8, -108) * mm, "end": v(-15.8, -122.2) * mm});
            skArc(sketch, "E92.MirrorCS", {"start": v(14.13, -120.3) * mm, "mid": v(0.12, -136.22) * mm, "end": v(-15.8, -122.2) * mm});
            skCircle(sketch, "E93.MirrorC", {"center": v(0, -120) * mm, "radius": 6 * mm});
            skSolve(sketch);
        }
        {
            var Q0;
            Q0=makeQuery(id+"F16.imprint","IMPRINT",FACE,{"disambiguationData":[TD([[makeQuery(id+"F16.imprint","IMPRINT",EDGE,{"derivedFrom":sQuery(id+"F16.wireOp",EDGE,"E80")}),-1.0]])]});
            var Q1;
            Q1=makeQuery(id+"F16.imprint","IMPRINT",FACE,{"disambiguationData":[TD([[makeQuery(id+"F16.imprint","IMPRINT",EDGE,{"derivedFrom":makeQuery(id+"F1.opExtrude","CAP_EDGE",EDGE,{"disambiguationData":[OSD([sQuery(id+"F0.wireOp",EDGE,"E4")])],"isStart":true})}),-1.0]])]});
            var Q2;
            Q2=makeQuery(id+"F16.imprint","IMPRINT",FACE,{"disambiguationData":[TD([[makeQuery(id+"F16.imprint","IMPRINT",EDGE,{"derivedFrom":makeQuery(id+"F1.opExtrude","CAP_EDGE",EDGE,{"disambiguationData":[OSD([sQuery(id+"F0.wireOp",EDGE,"E6")])],"isStart":true})}),-1.0]])]});
            var Q3;
            {var subQ1=sQuery(id+"F16.wireOp",EDGE,"E87.MirrorCS");Q3=makeQuery(id+"F16.imprint","IMPRINT",FACE,{"disambiguationData":[TD([[makeQuery(id+"F16.imprint","IMPRINT",EDGE,{"derivedFrom":subQ1}),1.0]])]});}
            extrude(context, id + "F17", {"entities" : qUnion([Q0, Q1, Q2, Q3]), "operationType" : NewBodyOperationType.ADD, "depth" : 25 * mm, "offsetDistance" : 25 * mm});
        }
    });
